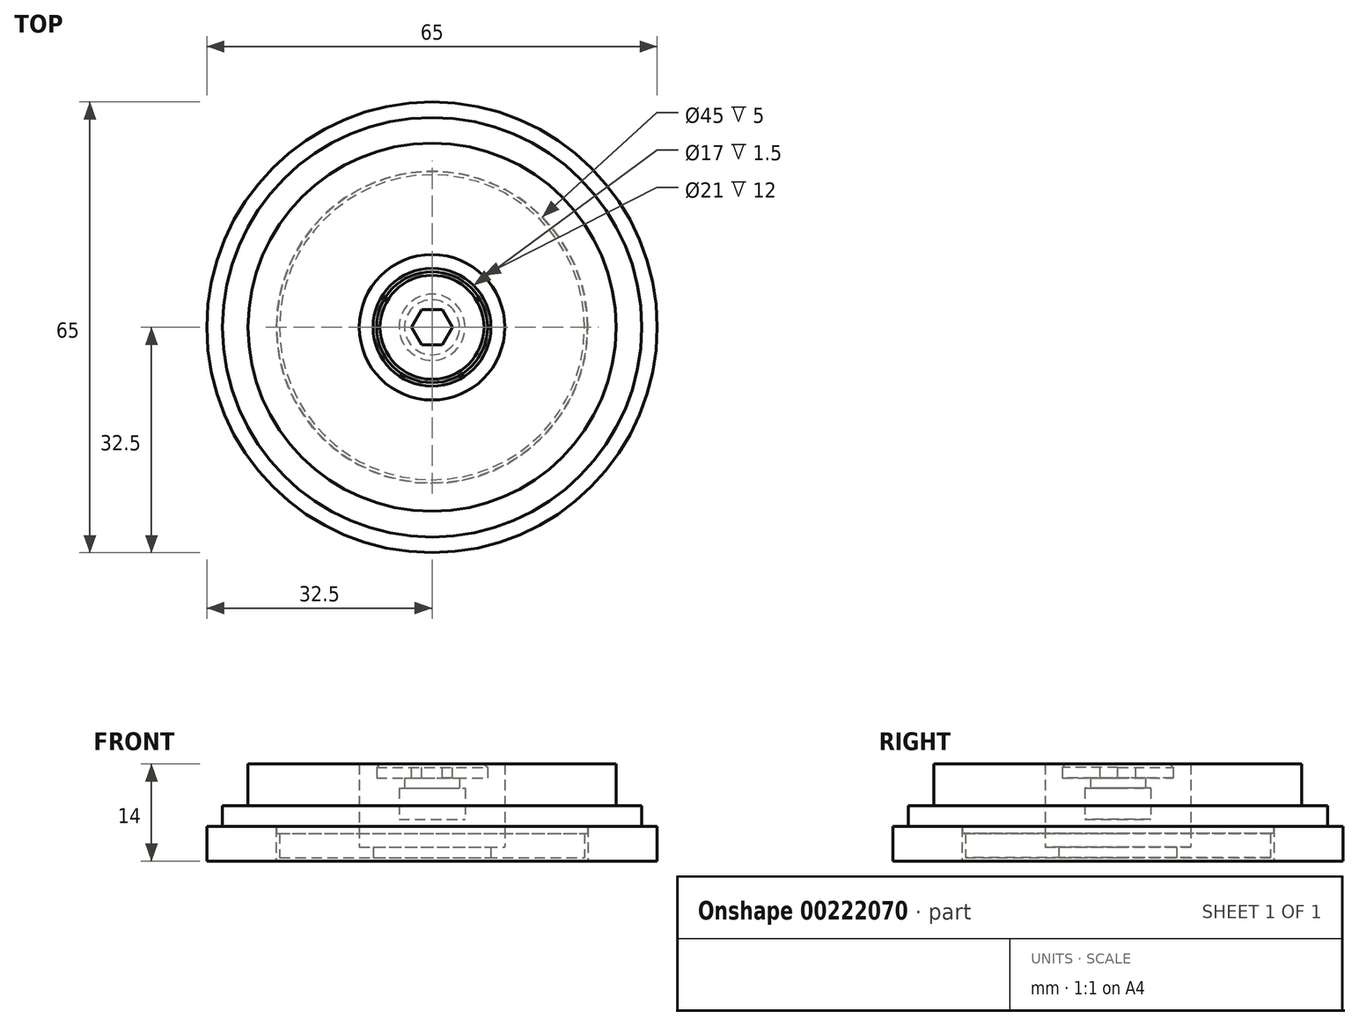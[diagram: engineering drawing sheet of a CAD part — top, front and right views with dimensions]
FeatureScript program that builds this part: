
annotation { "Feature Type Name" : "Feature", "Feature Type Description" : "" }
export const myFeature = defineFeature(function(context is Context, id is Id, definition is map)
    precondition{}
    {
        {
            var Q0;
            Q0=qCreatedBy(makeId("Front.planeOp"),FACE);
            var sketch = newSketch(context, id + "F0", { "sketchPlane" : qUnion([Q0])});
            skLineSegment(sketch, "E0.right", {"start": v(-32.5, -14) * mm, "end": v(-32.5, -9) * mm});
            skPoint(sketch, "E0.middle", {"position": v(0, -12) * mm});
            skLineSegment(sketch, "E1.bottom", {"start": v(-5.97, -14) * mm, "end": v(-22.5, -14) * mm});
            skLineSegment(sketch, "E1.right", {"start": v(-22.5, -14) * mm, "end": v(-22.5, -9) * mm});
            skLineSegment(sketch, "E2.right", {"start": v(-10.5, -12) * mm, "end": v(-10.5, -7) * mm});
            skPoint(sketch, "E2.middle", {"position": v(0, -20.75) * mm});
            skLineSegment(sketch, "E3.right", {"start": v(-6, -7) * mm, "end": v(-6, -12) * mm});
            skPoint(sketch, "E4", {"position": v(0, -21.25) * mm});
            skLineSegment(sketch, "E5.right", {"start": v(-10.5, -7) * mm, "end": v(-10.5, -2) * mm});
            skPoint(sketch, "E5.middle", {"position": v(0, -15.75) * mm});
            skLineSegment(sketch, "E6.right", {"start": v(-6, -8) * mm, "end": v(-6, -2) * mm});
            skLineSegment(sketch, "E7.bottom", {"start": v(0, -16) * mm, "end": v(-38.2, -16) * mm});
            skLineSegment(sketch, "E7.right", {"start": v(-38.2, -16) * mm, "end": v(-38.2, -6.5) * mm});
            skPoint(sketch, "E7.middle", {"position": v(0, -22.5) * mm});
            skLineSegment(sketch, "E8", {"start": v(-32.75, -6.5) * mm, "end": v(-32.75, -13) * mm});
            skLineSegment(sketch, "E9", {"start": v(-32.75, -13) * mm, "end": v(-32.56, -13) * mm});
            skPoint(sketch, "E10.start.orphan", {"position": v(-32.75, -14) * mm});
            skLineSegment(sketch, "E11.trimOffspring", {"start": v(-32.75, -6.5) * mm, "end": v(-38.2, -6.5) * mm});
            skLineSegment(sketch, "E12", {"start": v(0, -11.25) * mm, "end": v(0, -16) * mm});
            skLineSegment(sketch, "E13", {"start": v(-32.56, -13) * mm, "end": v(-32.56, -14) * mm});
            skLineSegment(sketch, "E14", {"start": v(-32.56, -14) * mm, "end": v(-32.5, -14) * mm});
            skPoint(sketch, "E15.orphan", {"position": v(-32.5, -13) * mm});
            skLineSegment(sketch, "E16", {"start": v(-22.44, -9) * mm, "end": v(-22.44, -10) * mm});
            skLineSegment(sketch, "E17", {"start": v(-22.44, -10) * mm, "end": v(-22, -10) * mm});
            skLineSegment(sketch, "E18", {"start": v(-22, -10) * mm, "end": v(-22, -13.5) * mm});
            skLineSegment(sketch, "E19", {"start": v(-22, -13.5) * mm, "end": v(-8.5, -13.5) * mm});
            skLineSegment(sketch, "E20", {"start": v(-8.5, -12) * mm, "end": v(-8.5, -13.5) * mm});
            skPoint(sketch, "E21.orphan", {"position": v(0, -13.5) * mm});
            skLineSegment(sketch, "E22", {"start": v(-30.25, -21.25) * mm, "end": v(-30.25, -6) * mm});
            skLineSegment(sketch, "E23", {"start": v(-10.5, -2) * mm, "end": v(-10.5, 0) * mm});
            skLineSegment(sketch, "E24.trimOffspring", {"start": v(-6, -2) * mm, "end": v(-10.5, -2) * mm});
            skLineSegment(sketch, "E25.trimOffspring", {"start": v(-26.55, -6) * mm, "end": v(-30.25, -6) * mm});
            skLineSegment(sketch, "E26.trimOffspring", {"start": v(-22.44, -9) * mm, "end": v(-22.5, -9) * mm});
            skLineSegment(sketch, "E27.trimOffspring", {"start": v(-22.44, -9) * mm, "end": v(-32.5, -9) * mm});
            skLineSegment(sketch, "E28.trimOffspring", {"start": v(-6, -7) * mm, "end": v(-10.5, -7) * mm});
            skLineSegment(sketch, "E29.trimOffspring", {"start": v(-6, -12) * mm, "end": v(-10.5, -12) * mm});
            skLineSegment(sketch, "E30.trimOffspring", {"start": v(-5.97, -14) * mm, "end": v(-32.5, -14) * mm});
            skLineSegment(sketch, "E31", {"start": v(-5.97, -14) * mm, "end": v(-5.97, -2.5) * mm});
            skLineSegment(sketch, "E32", {"start": v(-5.97, -2.5) * mm, "end": v(-3.97, -2.5) * mm});
            skLineSegment(sketch, "E33", {"start": v(-3.97, -16) * mm, "end": v(-3.97, -2.5) * mm});
            skLineSegment(sketch, "E34", {"start": v(-8, -2) * mm, "end": v(-8, 0) * mm});
            skLineSegment(sketch, "E35", {"start": v(-8, 0) * mm, "end": v(0, 0) * mm});
            skLineSegment(sketch, "E36", {"start": v(0, -11.25) * mm, "end": v(0, 0) * mm});
            skLineSegment(sketch, "E37", {"start": v(-6, -2) * mm, "end": v(-3.97, -2) * mm});
            skLineSegment(sketch, "E38", {"start": v(-3.97, -2) * mm, "end": v(-3.97, -2.5) * mm});
            skLineSegment(sketch, "E39.bottom", {"start": v(-43.25, -14.43) * mm, "end": v(-52.15, -14.43) * mm});
            skLineSegment(sketch, "E39.top", {"start": v(-43.25, -8.08) * mm, "end": v(-52.15, -8.08) * mm});
            skLineSegment(sketch, "E39.left", {"start": v(-43.25, -14.43) * mm, "end": v(-43.25, -8.08) * mm});
            skLineSegment(sketch, "E39.right", {"start": v(-52.15, -14.43) * mm, "end": v(-52.15, -8.08) * mm});
            skPoint(sketch, "E39.middle", {"position": v(-47.7, -11.25) * mm});
            skPoint(sketch, "E39.middle.positionSnap0", {"position": v(-38.2, -11.25) * mm});
            skPoint(sketch, "E39.centerSnap0", {"position": v(-38.2, -11.25) * mm});
            skLineSegment(sketch, "E40.bottom", {"start": v(-40.95, -14.43) * mm, "end": v(-54.45, -14.43) * mm});
            skLineSegment(sketch, "E40.top", {"start": v(-40.95, -15.53) * mm, "end": v(-54.45, -15.53) * mm});
            skLineSegment(sketch, "E40.left", {"start": v(-40.95, -14.43) * mm, "end": v(-40.95, -15.53) * mm});
            skLineSegment(sketch, "E40.right", {"start": v(-54.45, -14.43) * mm, "end": v(-54.45, -15.53) * mm});
            skPoint(sketch, "E40.middle", {"position": v(-47.7, -14.98) * mm});
            skPoint(sketch, "E40.middle.positionSnap0", {"position": v(-47.7, -14.43) * mm});
            skPoint(sketch, "E40.cornerSnap0", {"position": v(-47.7, -14.43) * mm});
            skPoint(sketch, "E40.centerSnap0", {"position": v(-47.7, -14.43) * mm});
            skLineSegment(sketch, "E41.bottom", {"start": v(-40.95, -8.08) * mm, "end": v(-54.45, -8.08) * mm});
            skLineSegment(sketch, "E41.top", {"start": v(-40.95, -2.08) * mm, "end": v(-54.45, -2.08) * mm});
            skLineSegment(sketch, "E41.left", {"start": v(-40.95, -8.08) * mm, "end": v(-40.95, -2.08) * mm});
            skLineSegment(sketch, "E41.right", {"start": v(-54.45, -8.08) * mm, "end": v(-54.45, -2.08) * mm});
            skPoint(sketch, "E41.middle", {"position": v(-47.7, -5.08) * mm});
            skPoint(sketch, "E41.middle.positionSnap0", {"position": v(-47.7, -8.08) * mm});
            skPoint(sketch, "E41.cornerSnap0", {"position": v(-47.7, -8.08) * mm});
            skPoint(sketch, "E41.centerSnap0", {"position": v(-47.7, -8.08) * mm});
            skLineSegment(sketch, "E42.MirrorCS", {"start": v(32.56, -14) * mm, "end": v(32.5, -14) * mm});
            skLineSegment(sketch, "E43.MirrorCS", {"start": v(22.44, -9) * mm, "end": v(22.5, -9) * mm});
            skLineSegment(sketch, "E44.MirrorCS", {"start": v(32.75, -13) * mm, "end": v(32.56, -13) * mm});
            skLineSegment(sketch, "E45.MirrorCS", {"start": v(3.97, -2) * mm, "end": v(3.97, -2.5) * mm});
            skLineSegment(sketch, "E46.MirrorCS", {"start": v(22.44, -10) * mm, "end": v(22, -10) * mm});
            skLineSegment(sketch, "E47.MirrorCS", {"start": v(6, -7) * mm, "end": v(10.5, -7) * mm});
            skPoint(sketch, "E48.MirrorP", {"position": v(32.75, -14) * mm});
            skLineSegment(sketch, "E49.MirrorCS", {"start": v(32.56, -13) * mm, "end": v(32.56, -14) * mm});
            skLineSegment(sketch, "E50.MirrorCS", {"start": v(6, -2) * mm, "end": v(3.97, -2) * mm});
            skLineSegment(sketch, "E51.MirrorCS", {"start": v(5.97, -2.5) * mm, "end": v(3.97, -2.5) * mm});
            skPoint(sketch, "E52.MirrorP", {"position": v(38.2, -11.25) * mm});
            skLineSegment(sketch, "E53.MirrorCS", {"start": v(38.2, -16) * mm, "end": v(38.2, -6.5) * mm});
            skLineSegment(sketch, "E54.MirrorCS", {"start": v(32.75, -6.5) * mm, "end": v(32.75, -13) * mm});
            skLineSegment(sketch, "E55.MirrorCS", {"start": v(32.75, -6.5) * mm, "end": v(38.2, -6.5) * mm});
            skLineSegment(sketch, "E56.MirrorCS", {"start": v(3.97, -16) * mm, "end": v(3.97, -2.5) * mm});
            skLineSegment(sketch, "E57.MirrorCS", {"start": v(22, -10) * mm, "end": v(22, -13.5) * mm});
            skLineSegment(sketch, "E58.MirrorCS", {"start": v(6, -12) * mm, "end": v(10.5, -12) * mm});
            skLineSegment(sketch, "E59.MirrorCS", {"start": v(8, -2) * mm, "end": v(8, 0) * mm});
            skLineSegment(sketch, "E60.MirrorCS", {"start": v(22, -13.5) * mm, "end": v(8.5, -13.5) * mm});
            skPoint(sketch, "E61.MirrorP", {"position": v(32.5, -13) * mm});
            skLineSegment(sketch, "E62.MirrorCS", {"start": v(22.44, -9) * mm, "end": v(32.5, -9) * mm});
            skLineSegment(sketch, "E63.MirrorCS", {"start": v(8.5, -12) * mm, "end": v(8.5, -13.5) * mm});
            skLineSegment(sketch, "E64.MirrorCS", {"start": v(22.5, -14) * mm, "end": v(22.5, -9) * mm});
            skLineSegment(sketch, "E65.MirrorCS", {"start": v(5.97, -14) * mm, "end": v(32.5, -14) * mm});
            skLineSegment(sketch, "E66.MirrorCS", {"start": v(6, -2) * mm, "end": v(10.5, -2) * mm});
            skLineSegment(sketch, "E67.MirrorCS", {"start": v(6, -7) * mm, "end": v(6, -12) * mm});
            skLineSegment(sketch, "E68.MirrorCS", {"start": v(22.44, -9) * mm, "end": v(22.44, -10) * mm});
            skLineSegment(sketch, "E69.MirrorCS", {"start": v(32.5, -14) * mm, "end": v(32.5, -9) * mm});
            skLineSegment(sketch, "E70.MirrorCS", {"start": v(5.97, -14) * mm, "end": v(22.5, -14) * mm});
            skLineSegment(sketch, "E71.MirrorCS", {"start": v(10.5, -12) * mm, "end": v(10.5, -7) * mm});
            skLineSegment(sketch, "E72.MirrorCS", {"start": v(10.5, -7) * mm, "end": v(10.5, -2) * mm});
            skLineSegment(sketch, "E73.MirrorCS", {"start": v(5.97, -14) * mm, "end": v(5.97, -2.5) * mm});
            skLineSegment(sketch, "E74.MirrorCS", {"start": v(6, -8) * mm, "end": v(6, -2) * mm});
            skLineSegment(sketch, "E75.MirrorCS", {"start": v(8, 0) * mm, "end": v(0, 0) * mm});
            skLineSegment(sketch, "E76.MirrorCS", {"start": v(0, -16) * mm, "end": v(38.2, -16) * mm});
            skLineSegment(sketch, "E77.bottom", {"start": v(-12.97, 105.59) * mm, "end": v(-55.27, 105.59) * mm});
            skLineSegment(sketch, "E77.top", {"start": v(-12.97, 153.59) * mm, "end": v(-55.27, 153.59) * mm});
            skLineSegment(sketch, "E77.left", {"start": v(-12.97, 105.59) * mm, "end": v(-12.97, 153.59) * mm});
            skLineSegment(sketch, "E77.right", {"start": v(-55.27, 105.59) * mm, "end": v(-55.27, 153.59) * mm});
            skPoint(sketch, "E77.middle", {"position": v(-34.12, 129.59) * mm});
            skLineSegment(sketch, "E78.top", {"start": v(-12.97, 157.59) * mm, "end": v(-55.27, 157.59) * mm});
            skLineSegment(sketch, "E78.left", {"start": v(-12.97, 153.59) * mm, "end": v(-12.97, 157.59) * mm});
            skLineSegment(sketch, "E78.right", {"start": v(-55.27, 153.59) * mm, "end": v(-55.27, 157.59) * mm});
            skLineSegment(sketch, "E79.bottom", {"start": v(3.88, 105.59) * mm, "end": v(-72.12, 105.59) * mm});
            skLineSegment(sketch, "E79.top", {"start": v(3.88, 89.59) * mm, "end": v(-72.12, 89.59) * mm});
            skLineSegment(sketch, "E79.left", {"start": v(3.88, 105.59) * mm, "end": v(3.88, 89.59) * mm});
            skLineSegment(sketch, "E79.right", {"start": v(-72.12, 105.59) * mm, "end": v(-72.12, 89.59) * mm});
            skPoint(sketch, "E79.middle", {"position": v(-34.12, 97.59) * mm});
            skPoint(sketch, "E79.middle.positionSnap0", {"position": v(-34.12, 105.59) * mm});
            skPoint(sketch, "E79.cornerSnap0", {"position": v(-34.12, 105.59) * mm});
            skPoint(sketch, "E79.centerSnap0", {"position": v(-34.12, 105.59) * mm});
            skCircle(sketch, "E80", {"center": v(62.43, 163.75) * mm, "radius": 11.5 * mm});
            skCircle(sketch, "E81", {"center": v(62.43, 138.35) * mm, "radius": 6.5 * mm});
            skLineSegment(sketch, "E82.bottom", {"start": v(41.28, 129.35) * mm, "end": v(83.58, 129.35) * mm});
            skLineSegment(sketch, "E82.top", {"start": v(41.28, 95.35) * mm, "end": v(83.58, 95.35) * mm});
            skLineSegment(sketch, "E82.left", {"start": v(41.28, 129.35) * mm, "end": v(41.28, 95.35) * mm});
            skLineSegment(sketch, "E82.right", {"start": v(83.58, 129.35) * mm, "end": v(83.58, 95.35) * mm});
            skPoint(sketch, "E82.middle", {"position": v(62.43, 112.35) * mm});
            skLineSegment(sketch, "E83", {"start": v(73.7, 161.49) * mm, "end": v(68.8, 137.07) * mm});
            skLineSegment(sketch, "E84", {"start": v(51.16, 161.49) * mm, "end": v(56.06, 137.07) * mm});
            skLineSegment(sketch, "E85.bottom", {"start": v(73.43, 129.35) * mm, "end": v(51.43, 129.35) * mm});
            skLineSegment(sketch, "E85.top", {"start": v(73.43, 131.35) * mm, "end": v(51.43, 131.35) * mm});
            skLineSegment(sketch, "E85.left", {"start": v(73.43, 129.35) * mm, "end": v(73.43, 131.35) * mm});
            skLineSegment(sketch, "E85.right", {"start": v(51.43, 129.35) * mm, "end": v(51.43, 131.35) * mm});
            skPoint(sketch, "E85.middle", {"position": v(62.43, 130.35) * mm});
            skPoint(sketch, "E85.middle.positionSnap0", {"position": v(62.43, 129.35) * mm});
            skPoint(sketch, "E85.centerSnap0", {"position": v(62.43, 129.35) * mm});
            skLineSegment(sketch, "E86.bottom", {"start": v(72.43, 131.85) * mm, "end": v(52.43, 131.85) * mm});
            skLineSegment(sketch, "E86.top", {"start": v(72.43, 149.85) * mm, "end": v(52.43, 149.85) * mm});
            skLineSegment(sketch, "E86.left", {"start": v(72.43, 131.85) * mm, "end": v(72.43, 149.85) * mm});
            skLineSegment(sketch, "E86.right", {"start": v(52.43, 131.85) * mm, "end": v(52.43, 149.85) * mm});
            skPoint(sketch, "E86.middle", {"position": v(62.43, 140.85) * mm});
            skCircle(sketch, "E87", {"center": v(62.43, 138.35) * mm, "radius": 5 * mm});
            skLineSegment(sketch, "E88.bottom", {"start": v(89.49, 129.35) * mm, "end": v(131.79, 129.35) * mm});
            skLineSegment(sketch, "E88.top", {"start": v(89.49, 95.35) * mm, "end": v(131.79, 95.35) * mm});
            skLineSegment(sketch, "E88.left", {"start": v(89.49, 129.35) * mm, "end": v(89.49, 95.35) * mm});
            skLineSegment(sketch, "E88.right", {"start": v(131.79, 129.35) * mm, "end": v(131.79, 95.35) * mm});
            skPoint(sketch, "E88.middle", {"position": v(110.64, 112.35) * mm});
            skLineSegment(sketch, "E89.bottom", {"start": v(121.64, 129.35) * mm, "end": v(99.64, 129.35) * mm});
            skLineSegment(sketch, "E89.top", {"start": v(121.64, 131.35) * mm, "end": v(99.64, 131.35) * mm});
            skLineSegment(sketch, "E89.left", {"start": v(121.64, 129.35) * mm, "end": v(121.64, 131.35) * mm});
            skLineSegment(sketch, "E89.right", {"start": v(99.64, 129.35) * mm, "end": v(99.64, 131.35) * mm});
            skPoint(sketch, "E89.middle", {"position": v(110.64, 130.35) * mm});
            skLineSegment(sketch, "E90.bottom", {"start": v(115.64, 131.35) * mm, "end": v(105.64, 131.35) * mm});
            skLineSegment(sketch, "E90.top", {"start": v(115.64, 170.62) * mm, "end": v(105.64, 170.62) * mm});
            skLineSegment(sketch, "E90.left", {"start": v(115.64, 131.35) * mm, "end": v(115.64, 170.62) * mm});
            skLineSegment(sketch, "E90.right", {"start": v(105.64, 131.35) * mm, "end": v(105.64, 170.62) * mm});
            skPoint(sketch, "E90.middle", {"position": v(110.64, 150.98) * mm});
            skLineSegment(sketch, "E91.bottom", {"start": v(120.64, 133.71) * mm, "end": v(100.64, 133.71) * mm});
            skLineSegment(sketch, "E91.top", {"start": v(120.64, 151.71) * mm, "end": v(100.64, 151.71) * mm});
            skLineSegment(sketch, "E91.left", {"start": v(120.64, 133.71) * mm, "end": v(120.64, 151.71) * mm});
            skLineSegment(sketch, "E91.right", {"start": v(100.64, 133.71) * mm, "end": v(100.64, 151.71) * mm});
            skPoint(sketch, "E91.middle", {"position": v(110.64, 142.71) * mm});
            skLineSegment(sketch, "E92.bottom", {"start": v(130.14, 133.71) * mm, "end": v(121.14, 133.71) * mm});
            skLineSegment(sketch, "E92.top", {"start": v(130.14, 169.32) * mm, "end": v(121.14, 169.32) * mm});
            skLineSegment(sketch, "E92.left", {"start": v(130.14, 133.71) * mm, "end": v(130.14, 169.32) * mm});
            skLineSegment(sketch, "E92.right", {"start": v(121.14, 133.71) * mm, "end": v(121.14, 169.32) * mm});
            skPoint(sketch, "E92.middle", {"position": v(125.64, 151.51) * mm});
            skLineSegment(sketch, "E93.bottom", {"start": v(122.14, 135.21) * mm, "end": v(125.14, 135.21) * mm});
            skLineSegment(sketch, "E93.top", {"start": v(122.14, 145.21) * mm, "end": v(125.14, 145.21) * mm});
            skLineSegment(sketch, "E93.left", {"start": v(122.14, 135.21) * mm, "end": v(122.14, 145.21) * mm});
            skLineSegment(sketch, "E93.right", {"start": v(125.14, 135.21) * mm, "end": v(125.14, 145.21) * mm});
            skPoint(sketch, "E93.middle", {"position": v(123.64, 140.21) * mm});
            skLineSegment(sketch, "E94.bottom", {"start": v(125.14, 135.21) * mm, "end": v(128.14, 135.21) * mm});
            skLineSegment(sketch, "E94.top", {"start": v(125.14, 145.21) * mm, "end": v(128.14, 145.21) * mm});
            skLineSegment(sketch, "E94.right", {"start": v(128.14, 135.21) * mm, "end": v(128.14, 145.21) * mm});
            skPoint(sketch, "E94.middle", {"position": v(126.64, 140.21) * mm});
            skPoint(sketch, "E94.middle.positionSnap0", {"position": v(125.14, 140.21) * mm});
            skPoint(sketch, "E94.centerSnap0", {"position": v(125.14, 140.21) * mm});
            skLineSegment(sketch, "E95", {"start": v(120.64, 140.21) * mm, "end": v(100.64, 140.21) * mm});
            skPoint(sketch, "E95.startSnap0", {"position": v(122.14, 140.21) * mm});
            skCircle(sketch, "E96", {"center": v(13.88, 100.59) * mm, "radius": 5 * mm});
            skCircle(sketch, "E97", {"center": v(13.88, 100.59) * mm, "radius": 6.5 * mm});
            skLineSegment(sketch, "E98", {"start": v(-6.7, 161.1) * mm, "end": v(-19.07, 120.65) * mm});
            skLineSegment(sketch, "E99", {"start": v(-19.07, 120.65) * mm, "end": v(13.45, 110.7) * mm});
            skLineSegment(sketch, "E100", {"start": v(13.45, 110.7) * mm, "end": v(25.82, 151.16) * mm});
            skLineSegment(sketch, "E101", {"start": v(25.82, 151.16) * mm, "end": v(-6.7, 161.1) * mm});
            skLineSegment(sketch, "E102", {"start": v(-19.07, 120.65) * mm, "end": v(-20.23, 116.83) * mm});
            skLineSegment(sketch, "E103", {"start": v(13.45, 110.7) * mm, "end": v(12.28, 106.88) * mm});
            skLineSegment(sketch, "E104", {"start": v(12.28, 106.88) * mm, "end": v(-20.23, 116.83) * mm});
            skLineSegment(sketch, "E105", {"start": v(-12.88, 140.88) * mm, "end": v(-14.8, 141.46) * mm});
            skLineSegment(sketch, "E106", {"start": v(-14.8, 141.46) * mm, "end": v(-18.01, 130.94) * mm});
            skLineSegment(sketch, "E107", {"start": v(-18.01, 130.94) * mm, "end": v(-16.1, 130.36) * mm});
            skLineSegment(sketch, "E108", {"start": v(-14.8, 141.46) * mm, "end": v(-11.58, 151.98) * mm});
            skLineSegment(sketch, "E109", {"start": v(-11.58, 151.98) * mm, "end": v(-9.67, 151.4) * mm});
            skLineSegment(sketch, "E110", {"start": v(-14.8, 141.46) * mm, "end": v(-52.1, 152.86) * mm});
            skCircle(sketch, "E111", {"center": v(-52.1, 152.86) * mm, "radius": 11.5 * mm});
            skLineSegment(sketch, "E112.top", {"start": v(-26.55, 54) * mm, "end": v(-68.85, 54) * mm});
            skLineSegment(sketch, "E112.right", {"start": v(-68.85, -6) * mm, "end": v(-68.85, 0) * mm});
            skPoint(sketch, "E112.middle", {"position": v(-47.7, 24) * mm});
            skPoint(sketch, "E112.middle.positionSnap0", {"position": v(-47.7, -2.08) * mm});
            skPoint(sketch, "E112.centerSnap0", {"position": v(-47.7, -2.08) * mm});
            skLineSegment(sketch, "E113.bottom", {"start": v(30.1, 3.82) * mm, "end": v(-19.05, 3.82) * mm});
            skLineSegment(sketch, "E113.top", {"start": v(30.1, 46.12) * mm, "end": v(-19.05, 46.12) * mm});
            skLineSegment(sketch, "E113.left", {"start": v(30.1, 3.82) * mm, "end": v(30.1, 46.12) * mm});
            skLineSegment(sketch, "E113.right", {"start": v(-19.05, 3.82) * mm, "end": v(-19.05, 46.12) * mm});
            skPoint(sketch, "E113.middle", {"position": v(5.53, 24.97) * mm});
            skLineSegment(sketch, "E114.left", {"start": v(-19.05, 46.12) * mm, "end": v(-19.05, 3.82) * mm});
            skLineSegment(sketch, "E114.right", {"start": v(-19.05, 47.02) * mm, "end": v(-19.05, 3.82) * mm});
            skLineSegment(sketch, "E115.bottom", {"start": v(30.1, 46.12) * mm, "end": v(37.6, 46.12) * mm});
            skLineSegment(sketch, "E115.top", {"start": v(30.1, 3.82) * mm, "end": v(37.6, 3.82) * mm});
            skLineSegment(sketch, "E115.left", {"start": v(30.1, 46.12) * mm, "end": v(30.1, 3.82) * mm});
            skLineSegment(sketch, "E115.right", {"start": v(37.6, 46.12) * mm, "end": v(37.6, 3.82) * mm});
            skLineSegment(sketch, "E116", {"start": v(-3.97, -2) * mm, "end": v(-3.97, -2) * mm});
            skLineSegment(sketch, "E117", {"start": v(-3.97, -2) * mm, "end": v(-3.97, -3.5) * mm});
            skLineSegment(sketch, "E118", {"start": v(-3.97, -3.5) * mm, "end": v(-4.76, -3.5) * mm});
            skLineSegment(sketch, "E119", {"start": v(-4.76, -3.5) * mm, "end": v(-4.76, -8) * mm});
            skLineSegment(sketch, "E120", {"start": v(-4.76, -8) * mm, "end": v(0, -8) * mm});
            skLineSegment(sketch, "E121", {"start": v(-26.55, -6) * mm, "end": v(-26.55, 0) * mm});
            skLineSegment(sketch, "E122", {"start": v(-10.5, 0) * mm, "end": v(-26.55, 0) * mm});
            skLineSegment(sketch, "E123.trimOffspring", {"start": v(-40.95, -6) * mm, "end": v(-68.85, -6) * mm});
            skSolve(sketch);
        }
        {
            var Q0;
            {var subQ6=sQuery(id+"F0.wireOp",EDGE,"E34");Q0=makeQuery(id+"F0.imprint","IMPRINT",FACE,{"disambiguationData":[TD([[makeQuery(id+"F0.imprint","IMPRINT",EDGE,{"derivedFrom":subQ6}),-1.0]])]});}
            var Q1;
            {var subQ0=sQuery(id+"F0.wireOp",EDGE,"E118");Q1=makeQuery(id+"F0.imprint","IMPRINT",FACE,{"disambiguationData":[TD([[makeQuery(id+"F0.imprint","IMPRINT",EDGE,{"derivedFrom":subQ0}),1.0]])]});}
            var Q2;
            Q2=sQuery(id+"F0.wireOp",EDGE,"E36");
            revolve(context, id + "F1", {"entities" : qUnion([Q0, Q1]), "axis" : qUnion([Q2]), "revolveType" : RevolveType.FULL});
        }
        {
            var Q0;
            Q0=makeQuery(id+"F1.opRevolve","SWEPT_FACE",FACE,{"disambiguationData":[OSD([sQuery(id+"F0.wireOp",EDGE,"E35")])]});
            var sketch = newSketch(context, id + "F2", { "sketchPlane" : qUnion([Q0])});
            skCircle(sketch, "E124.cCircle", {"center": v(0, 0) * mm, "radius": 2.56 * mm, "construction": true});
            skLineSegment(sketch, "E124.0", {"start": v(-1.48, 2.56) * mm, "end": v(1.48, 2.56) * mm});
            skLineSegment(sketch, "E124.1", {"start": v(1.48, 2.56) * mm, "end": v(2.96, 0) * mm});
            skLineSegment(sketch, "E124.2", {"start": v(2.96, 0) * mm, "end": v(1.48, -2.56) * mm});
            skLineSegment(sketch, "E124.3", {"start": v(1.48, -2.56) * mm, "end": v(-1.48, -2.56) * mm});
            skLineSegment(sketch, "E124.4", {"start": v(-1.48, -2.56) * mm, "end": v(-2.96, 0) * mm});
            skLineSegment(sketch, "E124.5", {"start": v(-2.96, 0) * mm, "end": v(-1.48, 2.56) * mm});
            skPoint(sketch, "E124.0.midPoint", {"position": v(0, 2.56) * mm});
            skSolve(sketch);
        }
        {
            var Q0;
            Q0=makeQuery(id+"F2.imprint","IMPRINT",FACE,{"disambiguationData":[TD([[makeQuery(id+"F2.imprint","IMPRINT",EDGE,{"derivedFrom":sQuery(id+"F2.wireOp",EDGE,"E124.0")}),-1.0]])]});
            extrude(context, id + "F3", {"entities" : qUnion([Q0]), "operationType" : NewBodyOperationType.REMOVE, "oppositeDirection" : true, "depth" : 2 * mm, "offsetDistance" : 25 * mm});
        }
        {
            var Q0;
            Q0=makeQuery(id+"F1.opRevolve","SWEPT_EDGE",EDGE,{"disambiguationData":[OSD([sQuery(id+"F0.wireOp",EDGE,"E34"),sQuery(id+"F0.wireOp",EDGE,"E35")])]});
            chamfer(context, id + "F4", {"entities" : qUnion([Q0]), "width" : .5 * mm, "tangentPropagation" : true});
        }
        {
            var Q0;
            {var subQ0=sQuery(id+"F0.wireOp",EDGE,"E2.right");Q0=makeQuery(id+"F0.imprint","IMPRINT",FACE,{"disambiguationData":[TD([[makeQuery(id+"F0.imprint","IMPRINT",EDGE,{"derivedFrom":subQ0}),1.0]])]});}
            var Q1;
            Q1=sQuery(id+"F0.wireOp",EDGE,"E36");
            revolve(context, id + "F5", {"operationType" : NewBodyOperationType.ADD, "entities" : qUnion([Q0]), "axis" : qUnion([Q1]), "revolveType" : RevolveType.FULL});
        }
        {
            var Q0;
            {var subQ0=sQuery(id+"F0.wireOp",EDGE,"E1.right");Q0=makeQuery(id+"F0.imprint","IMPRINT",FACE,{"disambiguationData":[TD([[makeQuery(id+"F0.imprint","IMPRINT",EDGE,{"derivedFrom":subQ0}),1.0]])]});}
            var Q1;
            {var subQ0=sQuery(id+"F0.wireOp",EDGE,"E0.right");Q1=makeQuery(id+"F0.imprint","IMPRINT",FACE,{"disambiguationData":[TD([[makeQuery(id+"F0.imprint","IMPRINT",EDGE,{"derivedFrom":subQ0}),-1.0]])]});}
            var Q2;
            Q2=sQuery(id+"F0.wireOp",EDGE,"E36");
            revolve(context, id + "F6", {"entities" : qUnion([Q0, Q1]), "axis" : qUnion([Q2]), "revolveType" : RevolveType.FULL});
        }
    });
